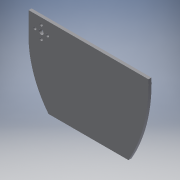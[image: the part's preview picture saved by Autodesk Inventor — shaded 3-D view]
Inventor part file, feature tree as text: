
AUTODESK INVENTOR PART (.ipt)
format: ipt  version: 2016 (Build 200138000, 138)  size: 104,960 bytes
history: native  units: in
note: dims shown in document units (in); Inventor stores cm internally (conversion verified against a paired STEP export)
features: reference x6, sketch x3, hole x2, extrude x1
ambient origin geometry x8: Origin, YZ Plane, XZ Plane, XY Plane, X Axis, Y Axis, Z Axis, Center Point
bodies: Solid1 (feature_tree)
feature tree (12):
  extrude  "Extrusion1"  Depth=4.0in
  hole  "Hole1"  [1 undecoded]
  hole  "Hole2"  [1 undecoded]
  sketch  "Sketch1"  dims[d0=6.0in d1=4.0in]
  sketch  "Sketch2"  dims[d2=1.0in d3=1.0in]
  reference  "Reference1"
  reference  "Reference2"
  reference  "Reference3"
  reference  "Reference4"
  reference  "Reference5"
  sketch  "Sketch3"  dims[d4=1.0in d5=0.15in d6=0.0in d7=0.1457in d8=0.75in d9=0.375in d10=0.25in d11=0.5635in d12=1.0in d13=0.8108in d14=0.2362in d15=0.75in d16=0.375in d17=0.25in d18=0.5635in d19=1.0in d20=0.8108in]
  reference  "Reference6"
note: 2 required parameter values undecoded (feature->parameter linkage not recoverable at this tier; creation-order binding heuristic only, values carry confidence <= 0.55)
